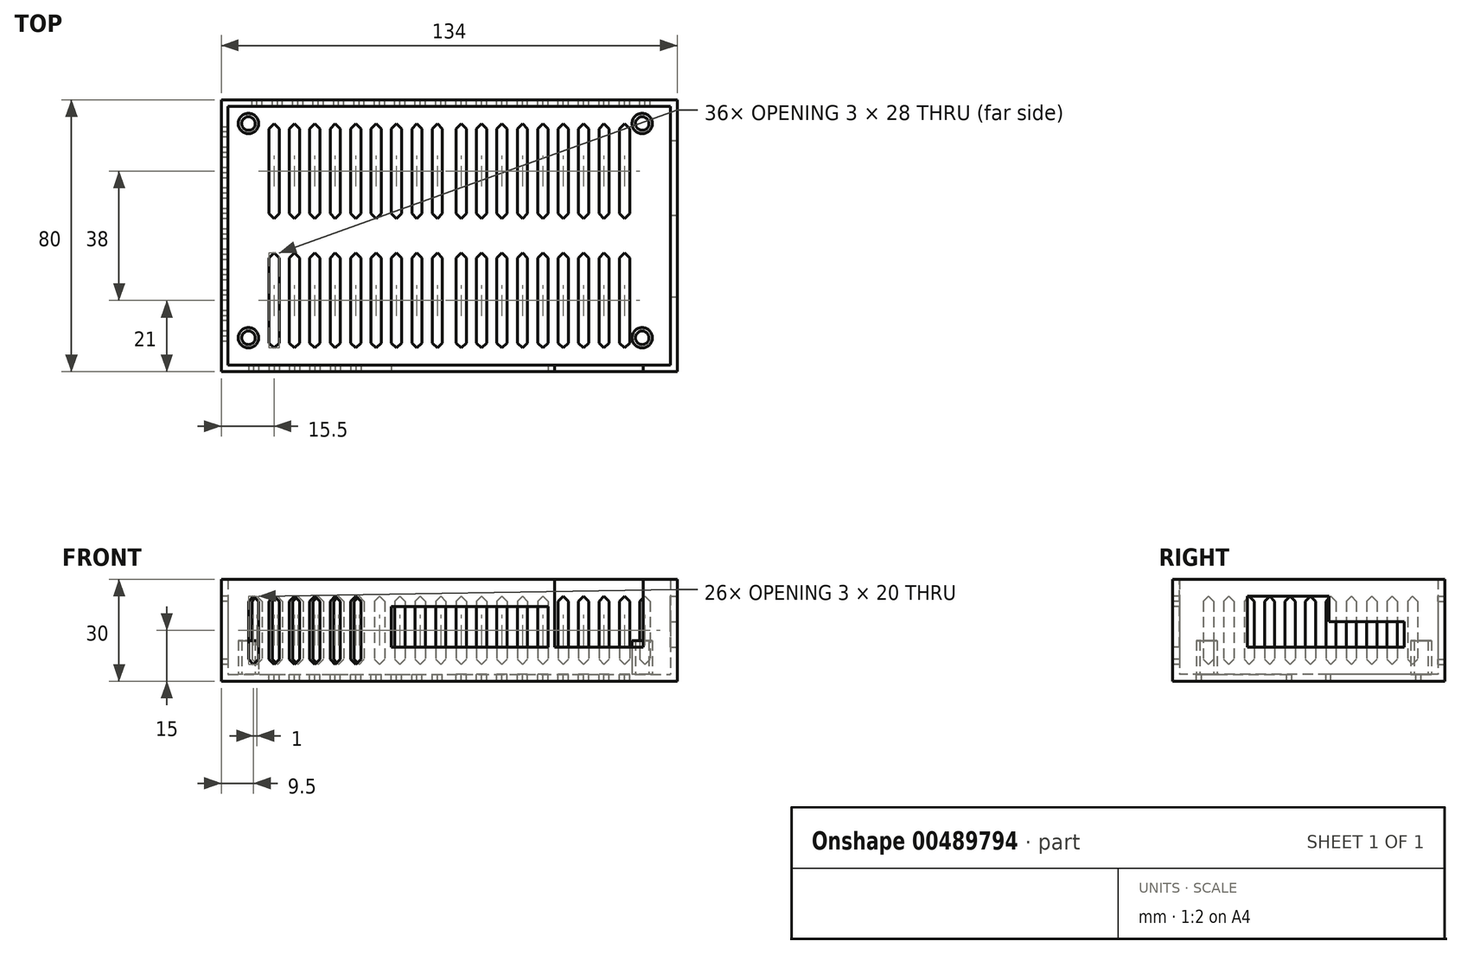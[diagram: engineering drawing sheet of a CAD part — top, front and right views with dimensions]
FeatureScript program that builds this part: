
annotation { "Feature Type Name" : "Feature", "Feature Type Description" : "" }
export const myFeature = defineFeature(function(context is Context, id is Id, definition is map)
    precondition{}
    {
        {
            var Q0;
            Q0=qCreatedBy(makeId("Top.planeOp"),FACE);
            var sketch = newSketch(context, id + "F0", { "sketchPlane" : qUnion([Q0])});
            skLineSegment(sketch, "E0.bottom", {"start": v(-65, 38) * mm, "end": v(65, 38) * mm});
            skLineSegment(sketch, "E0.top", {"start": v(-65, -38) * mm, "end": v(65, -38) * mm});
            skLineSegment(sketch, "E0.left", {"start": v(-65, 38) * mm, "end": v(-65, -38) * mm});
            skLineSegment(sketch, "E0.right", {"start": v(65, 38) * mm, "end": v(65, -38) * mm});
            skSolve(sketch);
        }
        {
            var Q0;
            Q0=makeQuery(id+"F0.imprint","IMPRINT",FACE,{"disambiguationData":[TD([[makeQuery(id+"F0.imprint","IMPRINT",EDGE,{"derivedFrom":sQuery(id+"F0.wireOp",EDGE,"E0.bottom")}),-1.0]])]});
            extrude(context, id + "F1", {"entities" : qUnion([Q0]), "depth" : 2 * mm});
        }
        {
            var Q0;
            Q0=qCreatedBy(makeId("Top.planeOp"),FACE);
            var sketch = newSketch(context, id + "F2", { "sketchPlane" : qUnion([Q0])});
            skLineSegment(sketch, "E1.bottom", {"start": v(-67, 40) * mm, "end": v(67, 40) * mm});
            skLineSegment(sketch, "E1.top", {"start": v(-67, -40) * mm, "end": v(67, -40) * mm});
            skLineSegment(sketch, "E1.left", {"start": v(-67, 40) * mm, "end": v(-67, -40) * mm});
            skLineSegment(sketch, "E1.right", {"start": v(67, 40) * mm, "end": v(67, -40) * mm});
            skLineSegment(sketch, "E2.bottom", {"start": v(-65, 38) * mm, "end": v(65, 38) * mm});
            skLineSegment(sketch, "E2.top", {"start": v(-65, -38) * mm, "end": v(65, -38) * mm});
            skLineSegment(sketch, "E2.left", {"start": v(-65, 38) * mm, "end": v(-65, -38) * mm});
            skLineSegment(sketch, "E2.right", {"start": v(65, 38) * mm, "end": v(65, -38) * mm});
            skSolve(sketch);
        }
        {
            var Q0;
            Q0=makeQuery(id+"F2.imprint","IMPRINT",FACE,{"disambiguationData":[TD([[makeQuery(id+"F2.imprint","IMPRINT",EDGE,{"derivedFrom":sQuery(id+"F2.wireOp",EDGE,"E1.bottom")}),-1.0]])]});
            extrude(context, id + "F3", {"entities" : qUnion([Q0]), "operationType" : NewBodyOperationType.ADD, "depth" : 30 * mm});
        }
        {
            var Q0;
            Q0=makeQuery(id+"F1.opExtrude","CAP_FACE",FACE,{"disambiguationData":[OSD([sQuery(id+"F0.wireOp",EDGE,"E0.bottom"),sQuery(id+"F0.wireOp",EDGE,"E0.top"),sQuery(id+"F0.wireOp",EDGE,"E0.left"),sQuery(id+"F0.wireOp",EDGE,"E0.right")])],"isStart":false});
            var sketch = newSketch(context, id + "F4", { "sketchPlane" : qUnion([Q0])});
            skCircle(sketch, "E3", {"center": v(-59, 33) * mm, "radius": 3 * mm});
            skCircle(sketch, "E4", {"center": v(56.7, 33) * mm, "radius": 3 * mm});
            skCircle(sketch, "E5", {"center": v(56.7, -30) * mm, "radius": 3 * mm});
            skCircle(sketch, "E6", {"center": v(-59, -30) * mm, "radius": 3 * mm});
            skCircle(sketch, "E7", {"center": v(-59, 33) * mm, "radius": 2 * mm});
            skCircle(sketch, "E8", {"center": v(-59, -30) * mm, "radius": 2 * mm});
            skCircle(sketch, "E9", {"center": v(56.7, -30) * mm, "radius": 2 * mm});
            skCircle(sketch, "E10", {"center": v(56.7, 33) * mm, "radius": 2 * mm});
            skSolve(sketch);
        }
        {
            var Q0;
            Q0=makeQuery(id+"F4.imprint","IMPRINT",FACE,{"disambiguationData":[TD([[makeQuery(id+"F4.imprint","IMPRINT",EDGE,{"derivedFrom":sQuery(id+"F4.wireOp",EDGE,"E4")}),1.0]])]});
            var Q1;
            Q1=makeQuery(id+"F4.imprint","IMPRINT",FACE,{"disambiguationData":[TD([[makeQuery(id+"F4.imprint","IMPRINT",EDGE,{"derivedFrom":sQuery(id+"F4.wireOp",EDGE,"E5")}),1.0]])]});
            var Q2;
            Q2=makeQuery(id+"F4.imprint","IMPRINT",FACE,{"disambiguationData":[TD([[makeQuery(id+"F4.imprint","IMPRINT",EDGE,{"derivedFrom":sQuery(id+"F4.wireOp",EDGE,"E6")}),1.0]])]});
            var Q3;
            Q3=makeQuery(id+"F4.imprint","IMPRINT",FACE,{"disambiguationData":[TD([[makeQuery(id+"F4.imprint","IMPRINT",EDGE,{"derivedFrom":sQuery(id+"F4.wireOp",EDGE,"E3")}),1.0]])]});
            extrude(context, id + "F5", {"entities" : qUnion([Q0, Q1, Q2, Q3]), "operationType" : NewBodyOperationType.ADD, "depth" : 10 * mm});
        }
        {
            var Q0;
            Q0=makeQuery(id+"F3.opExtrude","SWEPT_FACE",FACE,{"disambiguationData":[OSD([sQuery(id+"F2.wireOp",EDGE,"E1.top")])]});
            var sketch = newSketch(context, id + "F6", { "sketchPlane" : qUnion([Q0])});
            skLineSegment(sketch, "E11.bottom", {"start": v(31, 10) * mm, "end": v(57, 10) * mm});
            skLineSegment(sketch, "E11.top", {"start": v(31, 30) * mm, "end": v(57, 30) * mm});
            skLineSegment(sketch, "E11.left", {"start": v(31, 10) * mm, "end": v(31, 30) * mm});
            skLineSegment(sketch, "E11.right", {"start": v(57, 10) * mm, "end": v(57, 30) * mm});
            skLineSegment(sketch, "E12.bottom", {"start": v(-17, 10) * mm, "end": v(29, 10) * mm});
            skLineSegment(sketch, "E12.top", {"start": v(-17, 22) * mm, "end": v(29, 22) * mm});
            skLineSegment(sketch, "E12.left", {"start": v(-17, 10) * mm, "end": v(-17, 22) * mm});
            skLineSegment(sketch, "E12.right", {"start": v(29, 10) * mm, "end": v(29, 22) * mm});
            skSolve(sketch);
        }
        {
            var Q0;
            Q0=makeQuery(id+"F3.opExtrude","SWEPT_FACE",FACE,{"disambiguationData":[OSD([sQuery(id+"F2.wireOp",EDGE,"E1.right")])]});
            var sketch = newSketch(context, id + "F7", { "sketchPlane" : qUnion([Q0])});
            skLineSegment(sketch, "E13.bottom", {"start": v(-18, 10) * mm, "end": v(6, 10) * mm});
            skLineSegment(sketch, "E13.top", {"start": v(-18, 25) * mm, "end": v(6, 25) * mm});
            skLineSegment(sketch, "E13.left", {"start": v(-18, 10) * mm, "end": v(-18, 25) * mm});
            skLineSegment(sketch, "E13.right", {"start": v(6, 10) * mm, "end": v(6, 25) * mm});
            skLineSegment(sketch, "E14.bottom", {"start": v(6, 17.5) * mm, "end": v(28, 17.5) * mm});
            skLineSegment(sketch, "E14.top", {"start": v(6, 10) * mm, "end": v(28, 10) * mm});
            skLineSegment(sketch, "E14.left", {"start": v(6, 17.5) * mm, "end": v(6, 10) * mm});
            skLineSegment(sketch, "E14.right", {"start": v(28, 17.5) * mm, "end": v(28, 10) * mm});
            skSolve(sketch);
        }
        {
            var Q0;
            Q0=makeQuery(id+"F6.imprint","IMPRINT",FACE,{"disambiguationData":[TD([[makeQuery(id+"F6.imprint","IMPRINT",EDGE,{"derivedFrom":sQuery(id+"F6.wireOp",EDGE,"E11.bottom")}),1.0]])]});
            var Q1;
            Q1=makeQuery(id+"F6.imprint","IMPRINT",FACE,{"disambiguationData":[TD([[makeQuery(id+"F6.imprint","IMPRINT",EDGE,{"derivedFrom":sQuery(id+"F6.wireOp",EDGE,"E12.bottom")}),1.0]])]});
            extrude(context, id + "F8", {"entities" : qUnion([Q0, Q1]), "operationType" : NewBodyOperationType.REMOVE, "oppositeDirection" : true, "depth" : 2 * mm});
        }
        {
            var Q0;
            Q0=makeQuery(id+"F7.imprint","IMPRINT",FACE,{"disambiguationData":[TD([[makeQuery(id+"F7.imprint","IMPRINT",EDGE,{"derivedFrom":sQuery(id+"F7.wireOp",EDGE,"E13.bottom")}),1.0]])]});
            var Q1;
            Q1=makeQuery(id+"F7.imprint","IMPRINT",FACE,{"disambiguationData":[TD([[makeQuery(id+"F7.imprint","IMPRINT",EDGE,{"derivedFrom":sQuery(id+"F7.wireOp",EDGE,"E14.bottom")}),-1.0]])]});
            extrude(context, id + "F9", {"entities" : qUnion([Q0, Q1]), "operationType" : NewBodyOperationType.REMOVE, "oppositeDirection" : true, "depth" : 25 * mm});
        }
        {
            var Q0;
            Q0=makeQuery(id+"F3.opExtrude","SWEPT_FACE",FACE,{"disambiguationData":[OSD([sQuery(id+"F2.wireOp",EDGE,"E1.bottom")])]});
            var sketch = newSketch(context, id + "F10", { "sketchPlane" : qUnion([Q0])});
            skLineSegment(sketch, "E15.bottom", {"start": v(-59, 23.5) * mm, "end": v(-56, 23.5) * mm});
            skLineSegment(sketch, "E15.top", {"start": v(-59, 6.5) * mm, "end": v(-56, 6.5) * mm});
            skLineSegment(sketch, "E15.left", {"start": v(-59, 23.5) * mm, "end": v(-59, 6.5) * mm});
            skLineSegment(sketch, "E15.right", {"start": v(-56, 23.5) * mm, "end": v(-56, 6.5) * mm});
            skLineSegment(sketch, "E16", {"start": v(-59, 23.5) * mm, "end": v(-57.5, 25) * mm});
            skLineSegment(sketch, "E17", {"start": v(-57.5, 25) * mm, "end": v(-56, 23.5) * mm});
            skLineSegment(sketch, "E18", {"start": v(-56, 6.5) * mm, "end": v(-57.5, 5) * mm});
            skLineSegment(sketch, "E19", {"start": v(-57.5, 5) * mm, "end": v(-59, 6.5) * mm});
            skLineSegment(sketch, "E20.1.0.0", {"start": v(-53, 6.5) * mm, "end": v(-50, 6.5) * mm});
            skLineSegment(sketch, "E20.1.0.1", {"start": v(-50, 23.5) * mm, "end": v(-50, 6.5) * mm});
            skLineSegment(sketch, "E20.1.0.2", {"start": v(-53, 23.5) * mm, "end": v(-50, 23.5) * mm});
            skLineSegment(sketch, "E20.1.0.3", {"start": v(-53, 23.5) * mm, "end": v(-53, 6.5) * mm});
            skLineSegment(sketch, "E20.1.0.4", {"start": v(-51.5, 5) * mm, "end": v(-53, 6.5) * mm});
            skLineSegment(sketch, "E20.1.0.5", {"start": v(-53, 23.5) * mm, "end": v(-51.5, 25) * mm});
            skLineSegment(sketch, "E20.1.0.6", {"start": v(-51.5, 25) * mm, "end": v(-50, 23.5) * mm});
            skLineSegment(sketch, "E20.1.0.7", {"start": v(-50, 6.5) * mm, "end": v(-51.5, 5) * mm});
            skLineSegment(sketch, "E20.2.0.0", {"start": v(-47, 6.5) * mm, "end": v(-44, 6.5) * mm});
            skLineSegment(sketch, "E20.2.0.1", {"start": v(-44, 23.5) * mm, "end": v(-44, 6.5) * mm});
            skLineSegment(sketch, "E20.2.0.2", {"start": v(-47, 23.5) * mm, "end": v(-44, 23.5) * mm});
            skLineSegment(sketch, "E20.2.0.3", {"start": v(-47, 23.5) * mm, "end": v(-47, 6.5) * mm});
            skLineSegment(sketch, "E20.2.0.4", {"start": v(-45.5, 5) * mm, "end": v(-47, 6.5) * mm});
            skLineSegment(sketch, "E20.2.0.5", {"start": v(-47, 23.5) * mm, "end": v(-45.5, 25) * mm});
            skLineSegment(sketch, "E20.2.0.6", {"start": v(-45.5, 25) * mm, "end": v(-44, 23.5) * mm});
            skLineSegment(sketch, "E20.2.0.7", {"start": v(-44, 6.5) * mm, "end": v(-45.5, 5) * mm});
            skLineSegment(sketch, "E20.3.0.0", {"start": v(-41, 6.5) * mm, "end": v(-38, 6.5) * mm});
            skLineSegment(sketch, "E20.3.0.1", {"start": v(-38, 23.5) * mm, "end": v(-38, 6.5) * mm});
            skLineSegment(sketch, "E20.3.0.2", {"start": v(-41, 23.5) * mm, "end": v(-38, 23.5) * mm});
            skLineSegment(sketch, "E20.3.0.3", {"start": v(-41, 23.5) * mm, "end": v(-41, 6.5) * mm});
            skLineSegment(sketch, "E20.3.0.4", {"start": v(-39.5, 5) * mm, "end": v(-41, 6.5) * mm});
            skLineSegment(sketch, "E20.3.0.5", {"start": v(-41, 23.5) * mm, "end": v(-39.5, 25) * mm});
            skLineSegment(sketch, "E20.3.0.6", {"start": v(-39.5, 25) * mm, "end": v(-38, 23.5) * mm});
            skLineSegment(sketch, "E20.3.0.7", {"start": v(-38, 6.5) * mm, "end": v(-39.5, 5) * mm});
            skLineSegment(sketch, "E20.4.0.0", {"start": v(-35, 6.5) * mm, "end": v(-32, 6.5) * mm});
            skLineSegment(sketch, "E20.4.0.1", {"start": v(-32, 23.5) * mm, "end": v(-32, 6.5) * mm});
            skLineSegment(sketch, "E20.4.0.2", {"start": v(-35, 23.5) * mm, "end": v(-32, 23.5) * mm});
            skLineSegment(sketch, "E20.4.0.3", {"start": v(-35, 23.5) * mm, "end": v(-35, 6.5) * mm});
            skLineSegment(sketch, "E20.4.0.4", {"start": v(-33.5, 5) * mm, "end": v(-35, 6.5) * mm});
            skLineSegment(sketch, "E20.4.0.5", {"start": v(-35, 23.5) * mm, "end": v(-33.5, 25) * mm});
            skLineSegment(sketch, "E20.4.0.6", {"start": v(-33.5, 25) * mm, "end": v(-32, 23.5) * mm});
            skLineSegment(sketch, "E20.4.0.7", {"start": v(-32, 6.5) * mm, "end": v(-33.5, 5) * mm});
            skLineSegment(sketch, "E20.5.0.0", {"start": v(-29, 6.5) * mm, "end": v(-26, 6.5) * mm});
            skLineSegment(sketch, "E20.5.0.1", {"start": v(-26, 23.5) * mm, "end": v(-26, 6.5) * mm});
            skLineSegment(sketch, "E20.5.0.2", {"start": v(-29, 23.5) * mm, "end": v(-26, 23.5) * mm});
            skLineSegment(sketch, "E20.5.0.3", {"start": v(-29, 23.5) * mm, "end": v(-29, 6.5) * mm});
            skLineSegment(sketch, "E20.5.0.4", {"start": v(-27.5, 5) * mm, "end": v(-29, 6.5) * mm});
            skLineSegment(sketch, "E20.5.0.5", {"start": v(-29, 23.5) * mm, "end": v(-27.5, 25) * mm});
            skLineSegment(sketch, "E20.5.0.6", {"start": v(-27.5, 25) * mm, "end": v(-26, 23.5) * mm});
            skLineSegment(sketch, "E20.5.0.7", {"start": v(-26, 6.5) * mm, "end": v(-27.5, 5) * mm});
            skLineSegment(sketch, "E20.6.0.0", {"start": v(-23, 6.5) * mm, "end": v(-20, 6.5) * mm});
            skLineSegment(sketch, "E20.6.0.1", {"start": v(-20, 23.5) * mm, "end": v(-20, 6.5) * mm});
            skLineSegment(sketch, "E20.6.0.2", {"start": v(-23, 23.5) * mm, "end": v(-20, 23.5) * mm});
            skLineSegment(sketch, "E20.6.0.3", {"start": v(-23, 23.5) * mm, "end": v(-23, 6.5) * mm});
            skLineSegment(sketch, "E20.6.0.4", {"start": v(-21.5, 5) * mm, "end": v(-23, 6.5) * mm});
            skLineSegment(sketch, "E20.6.0.5", {"start": v(-23, 23.5) * mm, "end": v(-21.5, 25) * mm});
            skLineSegment(sketch, "E20.6.0.6", {"start": v(-21.5, 25) * mm, "end": v(-20, 23.5) * mm});
            skLineSegment(sketch, "E20.6.0.7", {"start": v(-20, 6.5) * mm, "end": v(-21.5, 5) * mm});
            skLineSegment(sketch, "E20.7.0.0", {"start": v(-17, 6.5) * mm, "end": v(-14, 6.5) * mm});
            skLineSegment(sketch, "E20.7.0.1", {"start": v(-14, 23.5) * mm, "end": v(-14, 6.5) * mm});
            skLineSegment(sketch, "E20.7.0.2", {"start": v(-17, 23.5) * mm, "end": v(-14, 23.5) * mm});
            skLineSegment(sketch, "E20.7.0.3", {"start": v(-17, 23.5) * mm, "end": v(-17, 6.5) * mm});
            skLineSegment(sketch, "E20.7.0.4", {"start": v(-15.5, 5) * mm, "end": v(-17, 6.5) * mm});
            skLineSegment(sketch, "E20.7.0.5", {"start": v(-17, 23.5) * mm, "end": v(-15.5, 25) * mm});
            skLineSegment(sketch, "E20.7.0.6", {"start": v(-15.5, 25) * mm, "end": v(-14, 23.5) * mm});
            skLineSegment(sketch, "E20.7.0.7", {"start": v(-14, 6.5) * mm, "end": v(-15.5, 5) * mm});
            skLineSegment(sketch, "E20.8.0.0", {"start": v(-11, 6.5) * mm, "end": v(-8, 6.5) * mm});
            skLineSegment(sketch, "E20.8.0.1", {"start": v(-8, 23.5) * mm, "end": v(-8, 6.5) * mm});
            skLineSegment(sketch, "E20.8.0.2", {"start": v(-11, 23.5) * mm, "end": v(-8, 23.5) * mm});
            skLineSegment(sketch, "E20.8.0.3", {"start": v(-11, 23.5) * mm, "end": v(-11, 6.5) * mm});
            skLineSegment(sketch, "E20.8.0.4", {"start": v(-9.5, 5) * mm, "end": v(-11, 6.5) * mm});
            skLineSegment(sketch, "E20.8.0.5", {"start": v(-11, 23.5) * mm, "end": v(-9.5, 25) * mm});
            skLineSegment(sketch, "E20.8.0.6", {"start": v(-9.5, 25) * mm, "end": v(-8, 23.5) * mm});
            skLineSegment(sketch, "E20.8.0.7", {"start": v(-8, 6.5) * mm, "end": v(-9.5, 5) * mm});
            skLineSegment(sketch, "E20.9.0.0", {"start": v(-5, 6.5) * mm, "end": v(-2, 6.5) * mm});
            skLineSegment(sketch, "E20.9.0.1", {"start": v(-2, 23.5) * mm, "end": v(-2, 6.5) * mm});
            skLineSegment(sketch, "E20.9.0.2", {"start": v(-5, 23.5) * mm, "end": v(-2, 23.5) * mm});
            skLineSegment(sketch, "E20.9.0.3", {"start": v(-5, 23.5) * mm, "end": v(-5, 6.5) * mm});
            skLineSegment(sketch, "E20.9.0.4", {"start": v(-3.5, 5) * mm, "end": v(-5, 6.5) * mm});
            skLineSegment(sketch, "E20.9.0.5", {"start": v(-5, 23.5) * mm, "end": v(-3.5, 25) * mm});
            skLineSegment(sketch, "E20.9.0.6", {"start": v(-3.5, 25) * mm, "end": v(-2, 23.5) * mm});
            skLineSegment(sketch, "E20.9.0.7", {"start": v(-2, 6.5) * mm, "end": v(-3.5, 5) * mm});
            skLineSegment(sketch, "E20.10.0.0", {"start": v(1, 6.5) * mm, "end": v(4, 6.5) * mm});
            skLineSegment(sketch, "E20.10.0.1", {"start": v(4, 23.5) * mm, "end": v(4, 6.5) * mm});
            skLineSegment(sketch, "E20.10.0.2", {"start": v(1, 23.5) * mm, "end": v(4, 23.5) * mm});
            skLineSegment(sketch, "E20.10.0.3", {"start": v(1, 23.5) * mm, "end": v(1, 6.5) * mm});
            skLineSegment(sketch, "E20.10.0.4", {"start": v(2.5, 5) * mm, "end": v(1, 6.5) * mm});
            skLineSegment(sketch, "E20.10.0.5", {"start": v(1, 23.5) * mm, "end": v(2.5, 25) * mm});
            skLineSegment(sketch, "E20.10.0.6", {"start": v(2.5, 25) * mm, "end": v(4, 23.5) * mm});
            skLineSegment(sketch, "E20.10.0.7", {"start": v(4, 6.5) * mm, "end": v(2.5, 5) * mm});
            skLineSegment(sketch, "E20.11.0.0", {"start": v(7, 6.5) * mm, "end": v(10, 6.5) * mm});
            skLineSegment(sketch, "E20.11.0.1", {"start": v(10, 23.5) * mm, "end": v(10, 6.5) * mm});
            skLineSegment(sketch, "E20.11.0.2", {"start": v(7, 23.5) * mm, "end": v(10, 23.5) * mm});
            skLineSegment(sketch, "E20.11.0.3", {"start": v(7, 23.5) * mm, "end": v(7, 6.5) * mm});
            skLineSegment(sketch, "E20.11.0.4", {"start": v(8.5, 5) * mm, "end": v(7, 6.5) * mm});
            skLineSegment(sketch, "E20.11.0.5", {"start": v(7, 23.5) * mm, "end": v(8.5, 25) * mm});
            skLineSegment(sketch, "E20.11.0.6", {"start": v(8.5, 25) * mm, "end": v(10, 23.5) * mm});
            skLineSegment(sketch, "E20.11.0.7", {"start": v(10, 6.5) * mm, "end": v(8.5, 5) * mm});
            skLineSegment(sketch, "E20.12.0.0", {"start": v(13, 6.5) * mm, "end": v(16, 6.5) * mm});
            skLineSegment(sketch, "E20.12.0.1", {"start": v(16, 23.5) * mm, "end": v(16, 6.5) * mm});
            skLineSegment(sketch, "E20.12.0.2", {"start": v(13, 23.5) * mm, "end": v(16, 23.5) * mm});
            skLineSegment(sketch, "E20.12.0.3", {"start": v(13, 23.5) * mm, "end": v(13, 6.5) * mm});
            skLineSegment(sketch, "E20.12.0.4", {"start": v(14.5, 5) * mm, "end": v(13, 6.5) * mm});
            skLineSegment(sketch, "E20.12.0.5", {"start": v(13, 23.5) * mm, "end": v(14.5, 25) * mm});
            skLineSegment(sketch, "E20.12.0.6", {"start": v(14.5, 25) * mm, "end": v(16, 23.5) * mm});
            skLineSegment(sketch, "E20.12.0.7", {"start": v(16, 6.5) * mm, "end": v(14.5, 5) * mm});
            skLineSegment(sketch, "E20.13.0.0", {"start": v(19, 6.5) * mm, "end": v(22, 6.5) * mm});
            skLineSegment(sketch, "E20.13.0.1", {"start": v(22, 23.5) * mm, "end": v(22, 6.5) * mm});
            skLineSegment(sketch, "E20.13.0.2", {"start": v(19, 23.5) * mm, "end": v(22, 23.5) * mm});
            skLineSegment(sketch, "E20.13.0.3", {"start": v(19, 23.5) * mm, "end": v(19, 6.5) * mm});
            skLineSegment(sketch, "E20.13.0.4", {"start": v(20.5, 5) * mm, "end": v(19, 6.5) * mm});
            skLineSegment(sketch, "E20.13.0.5", {"start": v(19, 23.5) * mm, "end": v(20.5, 25) * mm});
            skLineSegment(sketch, "E20.13.0.6", {"start": v(20.5, 25) * mm, "end": v(22, 23.5) * mm});
            skLineSegment(sketch, "E20.13.0.7", {"start": v(22, 6.5) * mm, "end": v(20.5, 5) * mm});
            skLineSegment(sketch, "E20.14.0.0", {"start": v(25, 6.5) * mm, "end": v(28, 6.5) * mm});
            skLineSegment(sketch, "E20.14.0.1", {"start": v(28, 23.5) * mm, "end": v(28, 6.5) * mm});
            skLineSegment(sketch, "E20.14.0.2", {"start": v(25, 23.5) * mm, "end": v(28, 23.5) * mm});
            skLineSegment(sketch, "E20.14.0.3", {"start": v(25, 23.5) * mm, "end": v(25, 6.5) * mm});
            skLineSegment(sketch, "E20.14.0.4", {"start": v(26.5, 5) * mm, "end": v(25, 6.5) * mm});
            skLineSegment(sketch, "E20.14.0.5", {"start": v(25, 23.5) * mm, "end": v(26.5, 25) * mm});
            skLineSegment(sketch, "E20.14.0.6", {"start": v(26.5, 25) * mm, "end": v(28, 23.5) * mm});
            skLineSegment(sketch, "E20.14.0.7", {"start": v(28, 6.5) * mm, "end": v(26.5, 5) * mm});
            skLineSegment(sketch, "E20.15.0.0", {"start": v(31, 6.5) * mm, "end": v(34, 6.5) * mm});
            skLineSegment(sketch, "E20.15.0.1", {"start": v(34, 23.5) * mm, "end": v(34, 6.5) * mm});
            skLineSegment(sketch, "E20.15.0.2", {"start": v(31, 23.5) * mm, "end": v(34, 23.5) * mm});
            skLineSegment(sketch, "E20.15.0.3", {"start": v(31, 23.5) * mm, "end": v(31, 6.5) * mm});
            skLineSegment(sketch, "E20.15.0.4", {"start": v(32.5, 5) * mm, "end": v(31, 6.5) * mm});
            skLineSegment(sketch, "E20.15.0.5", {"start": v(31, 23.5) * mm, "end": v(32.5, 25) * mm});
            skLineSegment(sketch, "E20.15.0.6", {"start": v(32.5, 25) * mm, "end": v(34, 23.5) * mm});
            skLineSegment(sketch, "E20.15.0.7", {"start": v(34, 6.5) * mm, "end": v(32.5, 5) * mm});
            skLineSegment(sketch, "E20.16.0.0", {"start": v(37, 6.5) * mm, "end": v(40, 6.5) * mm});
            skLineSegment(sketch, "E20.16.0.1", {"start": v(40, 23.5) * mm, "end": v(40, 6.5) * mm});
            skLineSegment(sketch, "E20.16.0.2", {"start": v(37, 23.5) * mm, "end": v(40, 23.5) * mm});
            skLineSegment(sketch, "E20.16.0.3", {"start": v(37, 23.5) * mm, "end": v(37, 6.5) * mm});
            skLineSegment(sketch, "E20.16.0.4", {"start": v(38.5, 5) * mm, "end": v(37, 6.5) * mm});
            skLineSegment(sketch, "E20.16.0.5", {"start": v(37, 23.5) * mm, "end": v(38.5, 25) * mm});
            skLineSegment(sketch, "E20.16.0.6", {"start": v(38.5, 25) * mm, "end": v(40, 23.5) * mm});
            skLineSegment(sketch, "E20.16.0.7", {"start": v(40, 6.5) * mm, "end": v(38.5, 5) * mm});
            skLineSegment(sketch, "E20.17.0.0", {"start": v(43, 6.5) * mm, "end": v(46, 6.5) * mm});
            skLineSegment(sketch, "E20.17.0.1", {"start": v(46, 23.5) * mm, "end": v(46, 6.5) * mm});
            skLineSegment(sketch, "E20.17.0.2", {"start": v(43, 23.5) * mm, "end": v(46, 23.5) * mm});
            skLineSegment(sketch, "E20.17.0.3", {"start": v(43, 23.5) * mm, "end": v(43, 6.5) * mm});
            skLineSegment(sketch, "E20.17.0.4", {"start": v(44.5, 5) * mm, "end": v(43, 6.5) * mm});
            skLineSegment(sketch, "E20.17.0.5", {"start": v(43, 23.5) * mm, "end": v(44.5, 25) * mm});
            skLineSegment(sketch, "E20.17.0.6", {"start": v(44.5, 25) * mm, "end": v(46, 23.5) * mm});
            skLineSegment(sketch, "E20.17.0.7", {"start": v(46, 6.5) * mm, "end": v(44.5, 5) * mm});
            skLineSegment(sketch, "E20.18.0.0", {"start": v(49, 6.5) * mm, "end": v(52, 6.5) * mm});
            skLineSegment(sketch, "E20.18.0.1", {"start": v(52, 23.5) * mm, "end": v(52, 6.5) * mm});
            skLineSegment(sketch, "E20.18.0.2", {"start": v(49, 23.5) * mm, "end": v(52, 23.5) * mm});
            skLineSegment(sketch, "E20.18.0.3", {"start": v(49, 23.5) * mm, "end": v(49, 6.5) * mm});
            skLineSegment(sketch, "E20.18.0.4", {"start": v(50.5, 5) * mm, "end": v(49, 6.5) * mm});
            skLineSegment(sketch, "E20.18.0.5", {"start": v(49, 23.5) * mm, "end": v(50.5, 25) * mm});
            skLineSegment(sketch, "E20.18.0.6", {"start": v(50.5, 25) * mm, "end": v(52, 23.5) * mm});
            skLineSegment(sketch, "E20.18.0.7", {"start": v(52, 6.5) * mm, "end": v(50.5, 5) * mm});
            skLineSegment(sketch, "E20.19.0.0", {"start": v(55, 6.5) * mm, "end": v(58, 6.5) * mm});
            skLineSegment(sketch, "E20.19.0.1", {"start": v(58, 23.5) * mm, "end": v(58, 6.5) * mm});
            skLineSegment(sketch, "E20.19.0.2", {"start": v(55, 23.5) * mm, "end": v(58, 23.5) * mm});
            skLineSegment(sketch, "E20.19.0.3", {"start": v(55, 23.5) * mm, "end": v(55, 6.5) * mm});
            skLineSegment(sketch, "E20.19.0.4", {"start": v(56.5, 5) * mm, "end": v(55, 6.5) * mm});
            skLineSegment(sketch, "E20.19.0.5", {"start": v(55, 23.5) * mm, "end": v(56.5, 25) * mm});
            skLineSegment(sketch, "E20.19.0.6", {"start": v(56.5, 25) * mm, "end": v(58, 23.5) * mm});
            skLineSegment(sketch, "E20.19.0.7", {"start": v(58, 6.5) * mm, "end": v(56.5, 5) * mm});
            skLineSegment(sketch, "E20.direction1", {"start": v(-57.5, 5) * mm, "end": v(-51.5, 5) * mm, "construction": true});
            skSolve(sketch);
        }
        {
            var Q0;
            Q0=qSketchRegion(id+"F10",true);
            extrude(context, id + "F11", {"entities" : qUnion([Q0]), "operationType" : NewBodyOperationType.REMOVE, "oppositeDirection" : true, "depth" : 2 * mm});
        }
        {
            var Q0;
            Q0=makeQuery(id+"F3.opExtrude","SWEPT_FACE",FACE,{"disambiguationData":[OSD([sQuery(id+"F2.wireOp",EDGE,"E1.left")])]});
            var sketch = newSketch(context, id + "F12", { "sketchPlane" : qUnion([Q0])});
            skLineSegment(sketch, "E21.bottom", {"start": v(-32, 23.5) * mm, "end": v(-29, 23.5) * mm});
            skLineSegment(sketch, "E21.top", {"start": v(-32, 6.5) * mm, "end": v(-29, 6.5) * mm});
            skLineSegment(sketch, "E21.left", {"start": v(-32, 23.5) * mm, "end": v(-32, 6.5) * mm});
            skLineSegment(sketch, "E21.right", {"start": v(-29, 23.5) * mm, "end": v(-29, 6.5) * mm});
            skLineSegment(sketch, "E22", {"start": v(-32, 23.5) * mm, "end": v(-30.5, 25) * mm});
            skLineSegment(sketch, "E23", {"start": v(-30.5, 25) * mm, "end": v(-29, 23.5) * mm});
            skLineSegment(sketch, "E24", {"start": v(-32, 6.5) * mm, "end": v(-30.5, 5) * mm});
            skLineSegment(sketch, "E25", {"start": v(-30.5, 5) * mm, "end": v(-29, 6.5) * mm});
            skLineSegment(sketch, "E26.1.0.0", {"start": v(-26, 23.5) * mm, "end": v(-23, 23.5) * mm});
            skLineSegment(sketch, "E26.1.0.1", {"start": v(-26, 6.5) * mm, "end": v(-23, 6.5) * mm});
            skLineSegment(sketch, "E26.1.0.2", {"start": v(-26, 23.5) * mm, "end": v(-26, 6.5) * mm});
            skLineSegment(sketch, "E26.1.0.3", {"start": v(-23, 23.5) * mm, "end": v(-23, 6.5) * mm});
            skLineSegment(sketch, "E26.1.0.4", {"start": v(-24.5, 5) * mm, "end": v(-23, 6.5) * mm});
            skLineSegment(sketch, "E26.1.0.5", {"start": v(-26, 23.5) * mm, "end": v(-24.5, 25) * mm});
            skLineSegment(sketch, "E26.1.0.6", {"start": v(-26, 6.5) * mm, "end": v(-24.5, 5) * mm});
            skLineSegment(sketch, "E26.1.0.7", {"start": v(-24.5, 25) * mm, "end": v(-23, 23.5) * mm});
            skLineSegment(sketch, "E26.2.0.0", {"start": v(-20, 23.5) * mm, "end": v(-17, 23.5) * mm});
            skLineSegment(sketch, "E26.2.0.1", {"start": v(-20, 6.5) * mm, "end": v(-17, 6.5) * mm});
            skLineSegment(sketch, "E26.2.0.2", {"start": v(-20, 23.5) * mm, "end": v(-20, 6.5) * mm});
            skLineSegment(sketch, "E26.2.0.3", {"start": v(-17, 23.5) * mm, "end": v(-17, 6.5) * mm});
            skLineSegment(sketch, "E26.2.0.4", {"start": v(-18.5, 5) * mm, "end": v(-17, 6.5) * mm});
            skLineSegment(sketch, "E26.2.0.5", {"start": v(-20, 23.5) * mm, "end": v(-18.5, 25) * mm});
            skLineSegment(sketch, "E26.2.0.6", {"start": v(-20, 6.5) * mm, "end": v(-18.5, 5) * mm});
            skLineSegment(sketch, "E26.2.0.7", {"start": v(-18.5, 25) * mm, "end": v(-17, 23.5) * mm});
            skLineSegment(sketch, "E26.3.0.0", {"start": v(-14, 23.5) * mm, "end": v(-11, 23.5) * mm});
            skLineSegment(sketch, "E26.3.0.1", {"start": v(-14, 6.5) * mm, "end": v(-11, 6.5) * mm});
            skLineSegment(sketch, "E26.3.0.2", {"start": v(-14, 23.5) * mm, "end": v(-14, 6.5) * mm});
            skLineSegment(sketch, "E26.3.0.3", {"start": v(-11, 23.5) * mm, "end": v(-11, 6.5) * mm});
            skLineSegment(sketch, "E26.3.0.4", {"start": v(-12.5, 5) * mm, "end": v(-11, 6.5) * mm});
            skLineSegment(sketch, "E26.3.0.5", {"start": v(-14, 23.5) * mm, "end": v(-12.5, 25) * mm});
            skLineSegment(sketch, "E26.3.0.6", {"start": v(-14, 6.5) * mm, "end": v(-12.5, 5) * mm});
            skLineSegment(sketch, "E26.3.0.7", {"start": v(-12.5, 25) * mm, "end": v(-11, 23.5) * mm});
            skLineSegment(sketch, "E26.4.0.0", {"start": v(-8, 23.5) * mm, "end": v(-5, 23.5) * mm});
            skLineSegment(sketch, "E26.4.0.1", {"start": v(-8, 6.5) * mm, "end": v(-5, 6.5) * mm});
            skLineSegment(sketch, "E26.4.0.2", {"start": v(-8, 23.5) * mm, "end": v(-8, 6.5) * mm});
            skLineSegment(sketch, "E26.4.0.3", {"start": v(-5, 23.5) * mm, "end": v(-5, 6.5) * mm});
            skLineSegment(sketch, "E26.4.0.4", {"start": v(-6.5, 5) * mm, "end": v(-5, 6.5) * mm});
            skLineSegment(sketch, "E26.4.0.5", {"start": v(-8, 23.5) * mm, "end": v(-6.5, 25) * mm});
            skLineSegment(sketch, "E26.4.0.6", {"start": v(-8, 6.5) * mm, "end": v(-6.5, 5) * mm});
            skLineSegment(sketch, "E26.4.0.7", {"start": v(-6.5, 25) * mm, "end": v(-5, 23.5) * mm});
            skLineSegment(sketch, "E26.5.0.0", {"start": v(-2, 23.5) * mm, "end": v(1, 23.5) * mm});
            skLineSegment(sketch, "E26.5.0.1", {"start": v(-2, 6.5) * mm, "end": v(1, 6.5) * mm});
            skLineSegment(sketch, "E26.5.0.2", {"start": v(-2, 23.5) * mm, "end": v(-2, 6.5) * mm});
            skLineSegment(sketch, "E26.5.0.3", {"start": v(1, 23.5) * mm, "end": v(1, 6.5) * mm});
            skLineSegment(sketch, "E26.5.0.4", {"start": v(-0.5, 5) * mm, "end": v(1, 6.5) * mm});
            skLineSegment(sketch, "E26.5.0.5", {"start": v(-2, 23.5) * mm, "end": v(-0.5, 25) * mm});
            skLineSegment(sketch, "E26.5.0.6", {"start": v(-2, 6.5) * mm, "end": v(-0.5, 5) * mm});
            skLineSegment(sketch, "E26.5.0.7", {"start": v(-0.5, 25) * mm, "end": v(1, 23.5) * mm});
            skLineSegment(sketch, "E26.6.0.0", {"start": v(4, 23.5) * mm, "end": v(7, 23.5) * mm});
            skLineSegment(sketch, "E26.6.0.1", {"start": v(4, 6.5) * mm, "end": v(7, 6.5) * mm});
            skLineSegment(sketch, "E26.6.0.2", {"start": v(4, 23.5) * mm, "end": v(4, 6.5) * mm});
            skLineSegment(sketch, "E26.6.0.3", {"start": v(7, 23.5) * mm, "end": v(7, 6.5) * mm});
            skLineSegment(sketch, "E26.6.0.4", {"start": v(5.5, 5) * mm, "end": v(7, 6.5) * mm});
            skLineSegment(sketch, "E26.6.0.5", {"start": v(4, 23.5) * mm, "end": v(5.5, 25) * mm});
            skLineSegment(sketch, "E26.6.0.6", {"start": v(4, 6.5) * mm, "end": v(5.5, 5) * mm});
            skLineSegment(sketch, "E26.6.0.7", {"start": v(5.5, 25) * mm, "end": v(7, 23.5) * mm});
            skLineSegment(sketch, "E26.7.0.0", {"start": v(10, 23.5) * mm, "end": v(13, 23.5) * mm});
            skLineSegment(sketch, "E26.7.0.1", {"start": v(10, 6.5) * mm, "end": v(13, 6.5) * mm});
            skLineSegment(sketch, "E26.7.0.2", {"start": v(10, 23.5) * mm, "end": v(10, 6.5) * mm});
            skLineSegment(sketch, "E26.7.0.3", {"start": v(13, 23.5) * mm, "end": v(13, 6.5) * mm});
            skLineSegment(sketch, "E26.7.0.4", {"start": v(11.5, 5) * mm, "end": v(13, 6.5) * mm});
            skLineSegment(sketch, "E26.7.0.5", {"start": v(10, 23.5) * mm, "end": v(11.5, 25) * mm});
            skLineSegment(sketch, "E26.7.0.6", {"start": v(10, 6.5) * mm, "end": v(11.5, 5) * mm});
            skLineSegment(sketch, "E26.7.0.7", {"start": v(11.5, 25) * mm, "end": v(13, 23.5) * mm});
            skLineSegment(sketch, "E26.8.0.0", {"start": v(16, 23.5) * mm, "end": v(19, 23.5) * mm});
            skLineSegment(sketch, "E26.8.0.1", {"start": v(16, 6.5) * mm, "end": v(19, 6.5) * mm});
            skLineSegment(sketch, "E26.8.0.2", {"start": v(16, 23.5) * mm, "end": v(16, 6.5) * mm});
            skLineSegment(sketch, "E26.8.0.3", {"start": v(19, 23.5) * mm, "end": v(19, 6.5) * mm});
            skLineSegment(sketch, "E26.8.0.4", {"start": v(17.5, 5) * mm, "end": v(19, 6.5) * mm});
            skLineSegment(sketch, "E26.8.0.5", {"start": v(16, 23.5) * mm, "end": v(17.5, 25) * mm});
            skLineSegment(sketch, "E26.8.0.6", {"start": v(16, 6.5) * mm, "end": v(17.5, 5) * mm});
            skLineSegment(sketch, "E26.8.0.7", {"start": v(17.5, 25) * mm, "end": v(19, 23.5) * mm});
            skLineSegment(sketch, "E26.9.0.0", {"start": v(22, 23.5) * mm, "end": v(25, 23.5) * mm});
            skLineSegment(sketch, "E26.9.0.1", {"start": v(22, 6.5) * mm, "end": v(25, 6.5) * mm});
            skLineSegment(sketch, "E26.9.0.2", {"start": v(22, 23.5) * mm, "end": v(22, 6.5) * mm});
            skLineSegment(sketch, "E26.9.0.3", {"start": v(25, 23.5) * mm, "end": v(25, 6.5) * mm});
            skLineSegment(sketch, "E26.9.0.4", {"start": v(23.5, 5) * mm, "end": v(25, 6.5) * mm});
            skLineSegment(sketch, "E26.9.0.5", {"start": v(22, 23.5) * mm, "end": v(23.5, 25) * mm});
            skLineSegment(sketch, "E26.9.0.6", {"start": v(22, 6.5) * mm, "end": v(23.5, 5) * mm});
            skLineSegment(sketch, "E26.9.0.7", {"start": v(23.5, 25) * mm, "end": v(25, 23.5) * mm});
            skLineSegment(sketch, "E26.10.0.0", {"start": v(28, 23.5) * mm, "end": v(31, 23.5) * mm});
            skLineSegment(sketch, "E26.10.0.1", {"start": v(28, 6.5) * mm, "end": v(31, 6.5) * mm});
            skLineSegment(sketch, "E26.10.0.2", {"start": v(28, 23.5) * mm, "end": v(28, 6.5) * mm});
            skLineSegment(sketch, "E26.10.0.3", {"start": v(31, 23.5) * mm, "end": v(31, 6.5) * mm});
            skLineSegment(sketch, "E26.10.0.4", {"start": v(29.5, 5) * mm, "end": v(31, 6.5) * mm});
            skLineSegment(sketch, "E26.10.0.5", {"start": v(28, 23.5) * mm, "end": v(29.5, 25) * mm});
            skLineSegment(sketch, "E26.10.0.6", {"start": v(28, 6.5) * mm, "end": v(29.5, 5) * mm});
            skLineSegment(sketch, "E26.10.0.7", {"start": v(29.5, 25) * mm, "end": v(31, 23.5) * mm});
            skLineSegment(sketch, "E26.direction1", {"start": v(-30.5, 5) * mm, "end": v(-24.5, 5) * mm, "construction": true});
            skSolve(sketch);
        }
        {
            var Q0;
            Q0=qSketchRegion(id+"F12",true);
            extrude(context, id + "F13", {"entities" : qUnion([Q0]), "operationType" : NewBodyOperationType.REMOVE, "oppositeDirection" : true, "depth" : 2 * mm});
        }
        {
            var Q0;
            Q0=makeQuery(id+"F3.opExtrude","SWEPT_FACE",FACE,{"disambiguationData":[OSD([sQuery(id+"F2.wireOp",EDGE,"E1.top")])]});
            var sketch = newSketch(context, id + "F14", { "sketchPlane" : qUnion([Q0])});
            skLineSegment(sketch, "E27.bottom", {"start": v(-59, 23.5) * mm, "end": v(-56, 23.5) * mm});
            skLineSegment(sketch, "E27.top", {"start": v(-59, 6.5) * mm, "end": v(-56, 6.5) * mm});
            skLineSegment(sketch, "E27.left", {"start": v(-59, 23.5) * mm, "end": v(-59, 6.5) * mm});
            skLineSegment(sketch, "E27.right", {"start": v(-56, 23.5) * mm, "end": v(-56, 6.5) * mm});
            skLineSegment(sketch, "E28", {"start": v(-59, 23.5) * mm, "end": v(-57.5, 25) * mm});
            skLineSegment(sketch, "E29", {"start": v(-57.5, 25) * mm, "end": v(-56, 23.5) * mm});
            skLineSegment(sketch, "E30", {"start": v(-59, 6.5) * mm, "end": v(-57.5, 5) * mm});
            skLineSegment(sketch, "E31", {"start": v(-57.5, 5) * mm, "end": v(-56, 6.5) * mm});
            skLineSegment(sketch, "E32.1.0.0", {"start": v(-53, 23.5) * mm, "end": v(-53, 6.5) * mm});
            skLineSegment(sketch, "E32.1.0.1", {"start": v(-50, 23.5) * mm, "end": v(-50, 6.5) * mm});
            skLineSegment(sketch, "E32.1.0.2", {"start": v(-53, 23.5) * mm, "end": v(-51.5, 25) * mm});
            skLineSegment(sketch, "E32.1.0.3", {"start": v(-53, 6.5) * mm, "end": v(-50, 6.5) * mm});
            skLineSegment(sketch, "E32.1.0.4", {"start": v(-53, 23.5) * mm, "end": v(-50, 23.5) * mm});
            skLineSegment(sketch, "E32.1.0.5", {"start": v(-51.5, 25) * mm, "end": v(-50, 23.5) * mm});
            skLineSegment(sketch, "E32.1.0.6", {"start": v(-53, 6.5) * mm, "end": v(-51.5, 5) * mm});
            skLineSegment(sketch, "E32.1.0.7", {"start": v(-51.5, 5) * mm, "end": v(-50, 6.5) * mm});
            skLineSegment(sketch, "E32.2.0.0", {"start": v(-47, 23.5) * mm, "end": v(-47, 6.5) * mm});
            skLineSegment(sketch, "E32.2.0.1", {"start": v(-44, 23.5) * mm, "end": v(-44, 6.5) * mm});
            skLineSegment(sketch, "E32.2.0.2", {"start": v(-47, 23.5) * mm, "end": v(-45.5, 25) * mm});
            skLineSegment(sketch, "E32.2.0.3", {"start": v(-47, 6.5) * mm, "end": v(-44, 6.5) * mm});
            skLineSegment(sketch, "E32.2.0.4", {"start": v(-47, 23.5) * mm, "end": v(-44, 23.5) * mm});
            skLineSegment(sketch, "E32.2.0.5", {"start": v(-45.5, 25) * mm, "end": v(-44, 23.5) * mm});
            skLineSegment(sketch, "E32.2.0.6", {"start": v(-47, 6.5) * mm, "end": v(-45.5, 5) * mm});
            skLineSegment(sketch, "E32.2.0.7", {"start": v(-45.5, 5) * mm, "end": v(-44, 6.5) * mm});
            skLineSegment(sketch, "E32.3.0.0", {"start": v(-41, 23.5) * mm, "end": v(-41, 6.5) * mm});
            skLineSegment(sketch, "E32.3.0.1", {"start": v(-38, 23.5) * mm, "end": v(-38, 6.5) * mm});
            skLineSegment(sketch, "E32.3.0.2", {"start": v(-41, 23.5) * mm, "end": v(-39.5, 25) * mm});
            skLineSegment(sketch, "E32.3.0.3", {"start": v(-41, 6.5) * mm, "end": v(-38, 6.5) * mm});
            skLineSegment(sketch, "E32.3.0.4", {"start": v(-41, 23.5) * mm, "end": v(-38, 23.5) * mm});
            skLineSegment(sketch, "E32.3.0.5", {"start": v(-39.5, 25) * mm, "end": v(-38, 23.5) * mm});
            skLineSegment(sketch, "E32.3.0.6", {"start": v(-41, 6.5) * mm, "end": v(-39.5, 5) * mm});
            skLineSegment(sketch, "E32.3.0.7", {"start": v(-39.5, 5) * mm, "end": v(-38, 6.5) * mm});
            skLineSegment(sketch, "E32.4.0.0", {"start": v(-35, 23.5) * mm, "end": v(-35, 6.5) * mm});
            skLineSegment(sketch, "E32.4.0.1", {"start": v(-32, 23.5) * mm, "end": v(-32, 6.5) * mm});
            skLineSegment(sketch, "E32.4.0.2", {"start": v(-35, 23.5) * mm, "end": v(-33.5, 25) * mm});
            skLineSegment(sketch, "E32.4.0.3", {"start": v(-35, 6.5) * mm, "end": v(-32, 6.5) * mm});
            skLineSegment(sketch, "E32.4.0.4", {"start": v(-35, 23.5) * mm, "end": v(-32, 23.5) * mm});
            skLineSegment(sketch, "E32.4.0.5", {"start": v(-33.5, 25) * mm, "end": v(-32, 23.5) * mm});
            skLineSegment(sketch, "E32.4.0.6", {"start": v(-35, 6.5) * mm, "end": v(-33.5, 5) * mm});
            skLineSegment(sketch, "E32.4.0.7", {"start": v(-33.5, 5) * mm, "end": v(-32, 6.5) * mm});
            skLineSegment(sketch, "E32.5.0.0", {"start": v(-29, 23.5) * mm, "end": v(-29, 6.5) * mm});
            skLineSegment(sketch, "E32.5.0.1", {"start": v(-26, 23.5) * mm, "end": v(-26, 6.5) * mm});
            skLineSegment(sketch, "E32.5.0.2", {"start": v(-29, 23.5) * mm, "end": v(-27.5, 25) * mm});
            skLineSegment(sketch, "E32.5.0.3", {"start": v(-29, 6.5) * mm, "end": v(-26, 6.5) * mm});
            skLineSegment(sketch, "E32.5.0.4", {"start": v(-29, 23.5) * mm, "end": v(-26, 23.5) * mm});
            skLineSegment(sketch, "E32.5.0.5", {"start": v(-27.5, 25) * mm, "end": v(-26, 23.5) * mm});
            skLineSegment(sketch, "E32.5.0.6", {"start": v(-29, 6.5) * mm, "end": v(-27.5, 5) * mm});
            skLineSegment(sketch, "E32.5.0.7", {"start": v(-27.5, 5) * mm, "end": v(-26, 6.5) * mm});
            skLineSegment(sketch, "E32.direction1", {"start": v(-57.5, 5) * mm, "end": v(-51.5, 5) * mm, "construction": true});
            skSolve(sketch);
        }
        {
            var Q0;
            Q0=qSketchRegion(id+"F14",true);
            extrude(context, id + "F15", {"entities" : qUnion([Q0]), "operationType" : NewBodyOperationType.REMOVE, "oppositeDirection" : true, "depth" : 2 * mm});
        }
        {
            var Q0;
            Q0=makeQuery(id+"F5.boolean.opBoolean","SPLIT",FACE,{"disambiguationData":[TD([makeQuery(id+"F3.opExtrude","SWEPT_FACE",FACE,{"disambiguationData":[OSD([sQuery(id+"F2.wireOp",EDGE,"E2.bottom")])]})])],"derivedFrom":makeQuery(id+"F1.opExtrude","CAP_FACE",FACE,{"disambiguationData":[OSD([sQuery(id+"F0.wireOp",EDGE,"E0.bottom"),sQuery(id+"F0.wireOp",EDGE,"E0.top"),sQuery(id+"F0.wireOp",EDGE,"E0.left"),sQuery(id+"F0.wireOp",EDGE,"E0.right")])],"isStart":false})});
            var sketch = newSketch(context, id + "F16", { "sketchPlane" : qUnion([Q0])});
            skLineSegment(sketch, "E33.bottom", {"start": v(-53, 31.5) * mm, "end": v(-50, 31.5) * mm});
            skLineSegment(sketch, "E33.top", {"start": v(-53, 6.5) * mm, "end": v(-50, 6.5) * mm});
            skLineSegment(sketch, "E33.left", {"start": v(-53, 31.5) * mm, "end": v(-53, 6.5) * mm});
            skLineSegment(sketch, "E33.right", {"start": v(-50, 31.5) * mm, "end": v(-50, 6.5) * mm});
            skLineSegment(sketch, "E34", {"start": v(-53, 6.5) * mm, "end": v(-51.5, 5) * mm});
            skLineSegment(sketch, "E35", {"start": v(-51.5, 5) * mm, "end": v(-50, 6.5) * mm});
            skLineSegment(sketch, "E36", {"start": v(-53, 31.5) * mm, "end": v(-51.5, 33) * mm});
            skLineSegment(sketch, "E37", {"start": v(-51.5, 33) * mm, "end": v(-50, 31.5) * mm});
            skLineSegment(sketch, "E38.1.0.0", {"start": v(-47, 31.5) * mm, "end": v(-47, 6.5) * mm});
            skLineSegment(sketch, "E38.1.0.1", {"start": v(-44, 31.5) * mm, "end": v(-44, 6.5) * mm});
            skLineSegment(sketch, "E38.1.0.2", {"start": v(-45.5, 33) * mm, "end": v(-44, 31.5) * mm});
            skLineSegment(sketch, "E38.1.0.3", {"start": v(-47, 31.5) * mm, "end": v(-44, 31.5) * mm});
            skLineSegment(sketch, "E38.1.0.4", {"start": v(-47, 6.5) * mm, "end": v(-44, 6.5) * mm});
            skLineSegment(sketch, "E38.1.0.5", {"start": v(-47, 6.5) * mm, "end": v(-45.5, 5) * mm});
            skLineSegment(sketch, "E38.1.0.6", {"start": v(-47, 31.5) * mm, "end": v(-45.5, 33) * mm});
            skLineSegment(sketch, "E38.1.0.7", {"start": v(-45.5, 5) * mm, "end": v(-44, 6.5) * mm});
            skLineSegment(sketch, "E38.2.0.0", {"start": v(-41, 31.5) * mm, "end": v(-41, 6.5) * mm});
            skLineSegment(sketch, "E38.2.0.1", {"start": v(-38, 31.5) * mm, "end": v(-38, 6.5) * mm});
            skLineSegment(sketch, "E38.2.0.2", {"start": v(-39.5, 33) * mm, "end": v(-38, 31.5) * mm});
            skLineSegment(sketch, "E38.2.0.3", {"start": v(-41, 31.5) * mm, "end": v(-38, 31.5) * mm});
            skLineSegment(sketch, "E38.2.0.4", {"start": v(-41, 6.5) * mm, "end": v(-38, 6.5) * mm});
            skLineSegment(sketch, "E38.2.0.5", {"start": v(-41, 6.5) * mm, "end": v(-39.5, 5) * mm});
            skLineSegment(sketch, "E38.2.0.6", {"start": v(-41, 31.5) * mm, "end": v(-39.5, 33) * mm});
            skLineSegment(sketch, "E38.2.0.7", {"start": v(-39.5, 5) * mm, "end": v(-38, 6.5) * mm});
            skLineSegment(sketch, "E38.3.0.0", {"start": v(-35, 31.5) * mm, "end": v(-35, 6.5) * mm});
            skLineSegment(sketch, "E38.3.0.1", {"start": v(-32, 31.5) * mm, "end": v(-32, 6.5) * mm});
            skLineSegment(sketch, "E38.3.0.2", {"start": v(-33.5, 33) * mm, "end": v(-32, 31.5) * mm});
            skLineSegment(sketch, "E38.3.0.3", {"start": v(-35, 31.5) * mm, "end": v(-32, 31.5) * mm});
            skLineSegment(sketch, "E38.3.0.4", {"start": v(-35, 6.5) * mm, "end": v(-32, 6.5) * mm});
            skLineSegment(sketch, "E38.3.0.5", {"start": v(-35, 6.5) * mm, "end": v(-33.5, 5) * mm});
            skLineSegment(sketch, "E38.3.0.6", {"start": v(-35, 31.5) * mm, "end": v(-33.5, 33) * mm});
            skLineSegment(sketch, "E38.3.0.7", {"start": v(-33.5, 5) * mm, "end": v(-32, 6.5) * mm});
            skLineSegment(sketch, "E38.4.0.0", {"start": v(-29, 31.5) * mm, "end": v(-29, 6.5) * mm});
            skLineSegment(sketch, "E38.4.0.1", {"start": v(-26, 31.5) * mm, "end": v(-26, 6.5) * mm});
            skLineSegment(sketch, "E38.4.0.2", {"start": v(-27.5, 33) * mm, "end": v(-26, 31.5) * mm});
            skLineSegment(sketch, "E38.4.0.3", {"start": v(-29, 31.5) * mm, "end": v(-26, 31.5) * mm});
            skLineSegment(sketch, "E38.4.0.4", {"start": v(-29, 6.5) * mm, "end": v(-26, 6.5) * mm});
            skLineSegment(sketch, "E38.4.0.5", {"start": v(-29, 6.5) * mm, "end": v(-27.5, 5) * mm});
            skLineSegment(sketch, "E38.4.0.6", {"start": v(-29, 31.5) * mm, "end": v(-27.5, 33) * mm});
            skLineSegment(sketch, "E38.4.0.7", {"start": v(-27.5, 5) * mm, "end": v(-26, 6.5) * mm});
            skLineSegment(sketch, "E38.5.0.0", {"start": v(-23, 31.5) * mm, "end": v(-23, 6.5) * mm});
            skLineSegment(sketch, "E38.5.0.1", {"start": v(-20, 31.5) * mm, "end": v(-20, 6.5) * mm});
            skLineSegment(sketch, "E38.5.0.2", {"start": v(-21.5, 33) * mm, "end": v(-20, 31.5) * mm});
            skLineSegment(sketch, "E38.5.0.3", {"start": v(-23, 31.5) * mm, "end": v(-20, 31.5) * mm});
            skLineSegment(sketch, "E38.5.0.4", {"start": v(-23, 6.5) * mm, "end": v(-20, 6.5) * mm});
            skLineSegment(sketch, "E38.5.0.5", {"start": v(-23, 6.5) * mm, "end": v(-21.5, 5) * mm});
            skLineSegment(sketch, "E38.5.0.6", {"start": v(-23, 31.5) * mm, "end": v(-21.5, 33) * mm});
            skLineSegment(sketch, "E38.5.0.7", {"start": v(-21.5, 5) * mm, "end": v(-20, 6.5) * mm});
            skLineSegment(sketch, "E38.6.0.0", {"start": v(-17, 31.5) * mm, "end": v(-17, 6.5) * mm});
            skLineSegment(sketch, "E38.6.0.1", {"start": v(-14, 31.5) * mm, "end": v(-14, 6.5) * mm});
            skLineSegment(sketch, "E38.6.0.2", {"start": v(-15.5, 33) * mm, "end": v(-14, 31.5) * mm});
            skLineSegment(sketch, "E38.6.0.3", {"start": v(-17, 31.5) * mm, "end": v(-14, 31.5) * mm});
            skLineSegment(sketch, "E38.6.0.4", {"start": v(-17, 6.5) * mm, "end": v(-14, 6.5) * mm});
            skLineSegment(sketch, "E38.6.0.5", {"start": v(-17, 6.5) * mm, "end": v(-15.5, 5) * mm});
            skLineSegment(sketch, "E38.6.0.6", {"start": v(-17, 31.5) * mm, "end": v(-15.5, 33) * mm});
            skLineSegment(sketch, "E38.6.0.7", {"start": v(-15.5, 5) * mm, "end": v(-14, 6.5) * mm});
            skLineSegment(sketch, "E38.7.0.0", {"start": v(-11, 31.5) * mm, "end": v(-11, 6.5) * mm});
            skLineSegment(sketch, "E38.7.0.1", {"start": v(-8, 31.5) * mm, "end": v(-8, 6.5) * mm});
            skLineSegment(sketch, "E38.7.0.2", {"start": v(-9.5, 33) * mm, "end": v(-8, 31.5) * mm});
            skLineSegment(sketch, "E38.7.0.3", {"start": v(-11, 31.5) * mm, "end": v(-8, 31.5) * mm});
            skLineSegment(sketch, "E38.7.0.4", {"start": v(-11, 6.5) * mm, "end": v(-8, 6.5) * mm});
            skLineSegment(sketch, "E38.7.0.5", {"start": v(-11, 6.5) * mm, "end": v(-9.5, 5) * mm});
            skLineSegment(sketch, "E38.7.0.6", {"start": v(-11, 31.5) * mm, "end": v(-9.5, 33) * mm});
            skLineSegment(sketch, "E38.7.0.7", {"start": v(-9.5, 5) * mm, "end": v(-8, 6.5) * mm});
            skLineSegment(sketch, "E38.8.0.0", {"start": v(-5, 31.5) * mm, "end": v(-5, 6.5) * mm});
            skLineSegment(sketch, "E38.8.0.1", {"start": v(-2, 31.5) * mm, "end": v(-2, 6.5) * mm});
            skLineSegment(sketch, "E38.8.0.2", {"start": v(-3.5, 33) * mm, "end": v(-2, 31.5) * mm});
            skLineSegment(sketch, "E38.8.0.3", {"start": v(-5, 31.5) * mm, "end": v(-2, 31.5) * mm});
            skLineSegment(sketch, "E38.8.0.4", {"start": v(-5, 6.5) * mm, "end": v(-2, 6.5) * mm});
            skLineSegment(sketch, "E38.8.0.5", {"start": v(-5, 6.5) * mm, "end": v(-3.5, 5) * mm});
            skLineSegment(sketch, "E38.8.0.6", {"start": v(-5, 31.5) * mm, "end": v(-3.5, 33) * mm});
            skLineSegment(sketch, "E38.8.0.7", {"start": v(-3.5, 5) * mm, "end": v(-2, 6.5) * mm});
            skLineSegment(sketch, "E38.direction1", {"start": v(-51.5, 5) * mm, "end": v(-45.5, 5) * mm, "construction": true});
            skLineSegment(sketch, "E39.MirrorCS", {"start": v(11, 6.5) * mm, "end": v(8, 6.5) * mm});
            skLineSegment(sketch, "E40.MirrorCS", {"start": v(53, 6.5) * mm, "end": v(51.5, 5) * mm});
            skLineSegment(sketch, "E41.MirrorCS", {"start": v(33.5, 33) * mm, "end": v(32, 31.5) * mm});
            skLineSegment(sketch, "E42.MirrorCS", {"start": v(51.5, 5) * mm, "end": v(50, 6.5) * mm});
            skLineSegment(sketch, "E43.MirrorCS", {"start": v(9.5, 33) * mm, "end": v(8, 31.5) * mm});
            skLineSegment(sketch, "E44.MirrorCS", {"start": v(27.5, 5) * mm, "end": v(26, 6.5) * mm});
            skLineSegment(sketch, "E45.MirrorCS", {"start": v(15.5, 5) * mm, "end": v(14, 6.5) * mm});
            skLineSegment(sketch, "E46.MirrorCS", {"start": v(53, 6.5) * mm, "end": v(50, 6.5) * mm});
            skLineSegment(sketch, "E47.MirrorCS", {"start": v(53, 31.5) * mm, "end": v(50, 31.5) * mm});
            skLineSegment(sketch, "E48.MirrorCS", {"start": v(35, 6.5) * mm, "end": v(32, 6.5) * mm});
            skLineSegment(sketch, "E49.MirrorCS", {"start": v(21.5, 33) * mm, "end": v(20, 31.5) * mm});
            skLineSegment(sketch, "E50.MirrorCS", {"start": v(53, 31.5) * mm, "end": v(51.5, 33) * mm});
            skLineSegment(sketch, "E51.MirrorCS", {"start": v(3.5, 5) * mm, "end": v(2, 6.5) * mm});
            skLineSegment(sketch, "E52.MirrorCS", {"start": v(41, 31.5) * mm, "end": v(38, 31.5) * mm});
            skLineSegment(sketch, "E53.MirrorCS", {"start": v(29, 31.5) * mm, "end": v(26, 31.5) * mm});
            skLineSegment(sketch, "E54.MirrorCS", {"start": v(39.5, 33) * mm, "end": v(38, 31.5) * mm});
            skLineSegment(sketch, "E55.MirrorCS", {"start": v(15.5, 33) * mm, "end": v(14, 31.5) * mm});
            skLineSegment(sketch, "E56.MirrorCS", {"start": v(45.5, 33) * mm, "end": v(44, 31.5) * mm});
            skLineSegment(sketch, "E57.MirrorCS", {"start": v(17, 6.5) * mm, "end": v(15.5, 5) * mm});
            skLineSegment(sketch, "E58.MirrorCS", {"start": v(47, 6.5) * mm, "end": v(45.5, 5) * mm});
            skLineSegment(sketch, "E59.MirrorCS", {"start": v(21.5, 5) * mm, "end": v(20, 6.5) * mm});
            skLineSegment(sketch, "E60.MirrorCS", {"start": v(23, 31.5) * mm, "end": v(20, 31.5) * mm});
            skLineSegment(sketch, "E61.MirrorCS", {"start": v(41, 6.5) * mm, "end": v(39.5, 5) * mm});
            skLineSegment(sketch, "E62.MirrorCS", {"start": v(5, 31.5) * mm, "end": v(2, 31.5) * mm});
            skLineSegment(sketch, "E63.MirrorCS", {"start": v(11, 6.5) * mm, "end": v(9.5, 5) * mm});
            skLineSegment(sketch, "E64.MirrorCS", {"start": v(5, 6.5) * mm, "end": v(2, 6.5) * mm});
            skLineSegment(sketch, "E65.MirrorCS", {"start": v(39.5, 5) * mm, "end": v(38, 6.5) * mm});
            skLineSegment(sketch, "E66.MirrorCS", {"start": v(47, 6.5) * mm, "end": v(44, 6.5) * mm});
            skLineSegment(sketch, "E67.MirrorCS", {"start": v(33.5, 5) * mm, "end": v(32, 6.5) * mm});
            skLineSegment(sketch, "E68.MirrorCS", {"start": v(41, 31.5) * mm, "end": v(39.5, 33) * mm});
            skLineSegment(sketch, "E69.MirrorCS", {"start": v(9.5, 5) * mm, "end": v(8, 6.5) * mm});
            skLineSegment(sketch, "E70.MirrorCS", {"start": v(5, 31.5) * mm, "end": v(3.5, 33) * mm});
            skLineSegment(sketch, "E71.MirrorCS", {"start": v(29, 6.5) * mm, "end": v(27.5, 5) * mm});
            skLineSegment(sketch, "E72.MirrorCS", {"start": v(47, 31.5) * mm, "end": v(44, 31.5) * mm});
            skLineSegment(sketch, "E73.MirrorCS", {"start": v(11, 31.5) * mm, "end": v(8, 31.5) * mm});
            skLineSegment(sketch, "E74.MirrorCS", {"start": v(35, 31.5) * mm, "end": v(32, 31.5) * mm});
            skLineSegment(sketch, "E75.MirrorCS", {"start": v(41, 6.5) * mm, "end": v(38, 6.5) * mm});
            skLineSegment(sketch, "E76.MirrorCS", {"start": v(17, 31.5) * mm, "end": v(14, 31.5) * mm});
            skLineSegment(sketch, "E77.MirrorCS", {"start": v(29, 6.5) * mm, "end": v(26, 6.5) * mm});
            skLineSegment(sketch, "E78.MirrorCS", {"start": v(29, 31.5) * mm, "end": v(27.5, 33) * mm});
            skLineSegment(sketch, "E79.MirrorCS", {"start": v(3.5, 33) * mm, "end": v(2, 31.5) * mm});
            skLineSegment(sketch, "E80.MirrorCS", {"start": v(5, 6.5) * mm, "end": v(3.5, 5) * mm});
            skLineSegment(sketch, "E81.MirrorCS", {"start": v(17, 31.5) * mm, "end": v(15.5, 33) * mm});
            skLineSegment(sketch, "E82.MirrorCS", {"start": v(17, 6.5) * mm, "end": v(14, 6.5) * mm});
            skLineSegment(sketch, "E83.MirrorCS", {"start": v(23, 6.5) * mm, "end": v(21.5, 5) * mm});
            skLineSegment(sketch, "E84.MirrorCS", {"start": v(23, 6.5) * mm, "end": v(20, 6.5) * mm});
            skLineSegment(sketch, "E85.MirrorCS", {"start": v(35, 6.5) * mm, "end": v(33.5, 5) * mm});
            skLineSegment(sketch, "E86.MirrorCS", {"start": v(11, 31.5) * mm, "end": v(9.5, 33) * mm});
            skLineSegment(sketch, "E87.MirrorCS", {"start": v(45.5, 5) * mm, "end": v(44, 6.5) * mm});
            skLineSegment(sketch, "E88.MirrorCS", {"start": v(51.5, 33) * mm, "end": v(50, 31.5) * mm});
            skLineSegment(sketch, "E89.MirrorCS", {"start": v(27.5, 33) * mm, "end": v(26, 31.5) * mm});
            skLineSegment(sketch, "E90.MirrorCS", {"start": v(47, 31.5) * mm, "end": v(45.5, 33) * mm});
            skLineSegment(sketch, "E91.MirrorCS", {"start": v(35, 31.5) * mm, "end": v(33.5, 33) * mm});
            skLineSegment(sketch, "E92.MirrorCS", {"start": v(23, 31.5) * mm, "end": v(21.5, 33) * mm});
            skLineSegment(sketch, "E93.MirrorCS", {"start": v(5, 31.5) * mm, "end": v(5, 6.5) * mm});
            skLineSegment(sketch, "E94.MirrorCS", {"start": v(50, 31.5) * mm, "end": v(50, 6.5) * mm});
            skLineSegment(sketch, "E95.MirrorCS", {"start": v(53, 31.5) * mm, "end": v(53, 6.5) * mm});
            skLineSegment(sketch, "E96.MirrorCS", {"start": v(29, 31.5) * mm, "end": v(29, 6.5) * mm});
            skLineSegment(sketch, "E97.MirrorCS", {"start": v(17, 31.5) * mm, "end": v(17, 6.5) * mm});
            skLineSegment(sketch, "E98.MirrorCS", {"start": v(14, 31.5) * mm, "end": v(14, 6.5) * mm});
            skLineSegment(sketch, "E99.MirrorCS", {"start": v(26, 31.5) * mm, "end": v(26, 6.5) * mm});
            skLineSegment(sketch, "E100.MirrorCS", {"start": v(38, 31.5) * mm, "end": v(38, 6.5) * mm});
            skLineSegment(sketch, "E101.MirrorCS", {"start": v(2, 31.5) * mm, "end": v(2, 6.5) * mm});
            skLineSegment(sketch, "E102.MirrorCS", {"start": v(8, 31.5) * mm, "end": v(8, 6.5) * mm});
            skLineSegment(sketch, "E103.MirrorCS", {"start": v(47, 31.5) * mm, "end": v(47, 6.5) * mm});
            skLineSegment(sketch, "E104.MirrorCS", {"start": v(44, 31.5) * mm, "end": v(44, 6.5) * mm});
            skLineSegment(sketch, "E105.MirrorCS", {"start": v(23, 31.5) * mm, "end": v(23, 6.5) * mm});
            skLineSegment(sketch, "E106.MirrorCS", {"start": v(11, 31.5) * mm, "end": v(11, 6.5) * mm});
            skLineSegment(sketch, "E107.MirrorCS", {"start": v(51.5, 5) * mm, "end": v(45.5, 5) * mm, "construction": true});
            skLineSegment(sketch, "E108.MirrorCS", {"start": v(35, 31.5) * mm, "end": v(35, 6.5) * mm});
            skLineSegment(sketch, "E109.MirrorCS", {"start": v(41, 31.5) * mm, "end": v(41, 6.5) * mm});
            skLineSegment(sketch, "E110.MirrorCS", {"start": v(20, 31.5) * mm, "end": v(20, 6.5) * mm});
            skLineSegment(sketch, "E111.MirrorCS", {"start": v(32, 31.5) * mm, "end": v(32, 6.5) * mm});
            skLineSegment(sketch, "E112.MirrorCS", {"start": v(-41, -6.5) * mm, "end": v(-39.5, -5) * mm});
            skLineSegment(sketch, "E113.MirrorCS", {"start": v(-45.5, -33) * mm, "end": v(-44, -31.5) * mm});
            skLineSegment(sketch, "E114.MirrorCS", {"start": v(-23, -6.5) * mm, "end": v(-21.5, -5) * mm});
            skLineSegment(sketch, "E115.MirrorCS", {"start": v(-5, -31.5) * mm, "end": v(-2, -31.5) * mm});
            skLineSegment(sketch, "E116.MirrorCS", {"start": v(21.5, -33) * mm, "end": v(20, -31.5) * mm});
            skLineSegment(sketch, "E117.MirrorCS", {"start": v(-11, -31.5) * mm, "end": v(-8, -31.5) * mm});
            skLineSegment(sketch, "E118.MirrorCS", {"start": v(-35, -6.5) * mm, "end": v(-33.5, -5) * mm});
            skLineSegment(sketch, "E119.MirrorCS", {"start": v(-47, -31.5) * mm, "end": v(-44, -31.5) * mm});
            skLineSegment(sketch, "E120.MirrorCS", {"start": v(-23, -31.5) * mm, "end": v(-20, -31.5) * mm});
            skLineSegment(sketch, "E121.MirrorCS", {"start": v(39.5, -5) * mm, "end": v(38, -6.5) * mm});
            skLineSegment(sketch, "E122.MirrorCS", {"start": v(17, -31.5) * mm, "end": v(15.5, -33) * mm});
            skLineSegment(sketch, "E123.MirrorCS", {"start": v(29, -31.5) * mm, "end": v(26, -31.5) * mm});
            skLineSegment(sketch, "E124.MirrorCS", {"start": v(-41, -31.5) * mm, "end": v(-38, -31.5) * mm});
            skLineSegment(sketch, "E125.MirrorCS", {"start": v(-29, -31.5) * mm, "end": v(-26, -31.5) * mm});
            skLineSegment(sketch, "E126.MirrorCS", {"start": v(-9.5, -5) * mm, "end": v(-8, -6.5) * mm});
            skLineSegment(sketch, "E127.MirrorCS", {"start": v(9.5, -33) * mm, "end": v(8, -31.5) * mm});
            skLineSegment(sketch, "E128.MirrorCS", {"start": v(35, -6.5) * mm, "end": v(33.5, -5) * mm});
            skLineSegment(sketch, "E129.MirrorCS", {"start": v(-17, -31.5) * mm, "end": v(-14, -31.5) * mm});
            skLineSegment(sketch, "E130.MirrorCS", {"start": v(-17, -6.5) * mm, "end": v(-14, -6.5) * mm});
            skLineSegment(sketch, "E131.MirrorCS", {"start": v(-29, -6.5) * mm, "end": v(-26, -6.5) * mm});
            skLineSegment(sketch, "E132.MirrorCS", {"start": v(-41, -6.5) * mm, "end": v(-38, -6.5) * mm});
            skLineSegment(sketch, "E133.MirrorCS", {"start": v(27.5, -33) * mm, "end": v(26, -31.5) * mm});
            skLineSegment(sketch, "E134.MirrorCS", {"start": v(9.5, -5) * mm, "end": v(8, -6.5) * mm});
            skLineSegment(sketch, "E135.MirrorCS", {"start": v(15.5, -5) * mm, "end": v(14, -6.5) * mm});
            skLineSegment(sketch, "E136.MirrorCS", {"start": v(41, -6.5) * mm, "end": v(39.5, -5) * mm});
            skLineSegment(sketch, "E137.MirrorCS", {"start": v(29, -6.5) * mm, "end": v(26, -6.5) * mm});
            skLineSegment(sketch, "E138.MirrorCS", {"start": v(-39.5, -5) * mm, "end": v(-38, -6.5) * mm});
            skLineSegment(sketch, "E139.MirrorCS", {"start": v(-33.5, -5) * mm, "end": v(-32, -6.5) * mm});
            skLineSegment(sketch, "E140.MirrorCS", {"start": v(-21.5, -5) * mm, "end": v(-20, -6.5) * mm});
            skLineSegment(sketch, "E141.MirrorCS", {"start": v(35, -31.5) * mm, "end": v(32, -31.5) * mm});
            skLineSegment(sketch, "E142.MirrorCS", {"start": v(47, -31.5) * mm, "end": v(45.5, -33) * mm});
            skLineSegment(sketch, "E143.MirrorCS", {"start": v(-23, -6.5) * mm, "end": v(-20, -6.5) * mm});
            skLineSegment(sketch, "E144.MirrorCS", {"start": v(39.5, -33) * mm, "end": v(38, -31.5) * mm});
            skLineSegment(sketch, "E145.MirrorCS", {"start": v(-11, -6.5) * mm, "end": v(-8, -6.5) * mm});
            skLineSegment(sketch, "E146.MirrorCS", {"start": v(51.5, -5) * mm, "end": v(50, -6.5) * mm});
            skLineSegment(sketch, "E147.MirrorCS", {"start": v(47, -6.5) * mm, "end": v(45.5, -5) * mm});
            skLineSegment(sketch, "E148.MirrorCS", {"start": v(-51.5, -5) * mm, "end": v(-45.5, -5) * mm, "construction": true});
            skLineSegment(sketch, "E149.MirrorCS", {"start": v(47, -31.5) * mm, "end": v(44, -31.5) * mm});
            skLineSegment(sketch, "E150.MirrorCS", {"start": v(11, -31.5) * mm, "end": v(8, -31.5) * mm});
            skLineSegment(sketch, "E151.MirrorCS", {"start": v(17, -6.5) * mm, "end": v(14, -6.5) * mm});
            skLineSegment(sketch, "E152.MirrorCS", {"start": v(-53, -31.5) * mm, "end": v(-51.5, -33) * mm});
            skLineSegment(sketch, "E153.MirrorCS", {"start": v(-35, -6.5) * mm, "end": v(-32, -6.5) * mm});
            skLineSegment(sketch, "E154.MirrorCS", {"start": v(47, -6.5) * mm, "end": v(44, -6.5) * mm});
            skLineSegment(sketch, "E155.MirrorCS", {"start": v(-3.5, -33) * mm, "end": v(-2, -31.5) * mm});
            skLineSegment(sketch, "E156.MirrorCS", {"start": v(35, -6.5) * mm, "end": v(32, -6.5) * mm});
            skLineSegment(sketch, "E157.MirrorCS", {"start": v(5, -6.5) * mm, "end": v(2, -6.5) * mm});
            skLineSegment(sketch, "E158.MirrorCS", {"start": v(5, -6.5) * mm, "end": v(3.5, -5) * mm});
            skLineSegment(sketch, "E159.MirrorCS", {"start": v(53, -31.5) * mm, "end": v(51.5, -33) * mm});
            skLineSegment(sketch, "E160.MirrorCS", {"start": v(-5, -6.5) * mm, "end": v(-2, -6.5) * mm});
            skLineSegment(sketch, "E161.MirrorCS", {"start": v(-39.5, -33) * mm, "end": v(-38, -31.5) * mm});
            skLineSegment(sketch, "E162.MirrorCS", {"start": v(-27.5, -33) * mm, "end": v(-26, -31.5) * mm});
            skLineSegment(sketch, "E163.MirrorCS", {"start": v(-21.5, -33) * mm, "end": v(-20, -31.5) * mm});
            skLineSegment(sketch, "E164.MirrorCS", {"start": v(-15.5, -33) * mm, "end": v(-14, -31.5) * mm});
            skLineSegment(sketch, "E165.MirrorCS", {"start": v(-9.5, -33) * mm, "end": v(-8, -31.5) * mm});
            skLineSegment(sketch, "E166.MirrorCS", {"start": v(21.5, -5) * mm, "end": v(20, -6.5) * mm});
            skLineSegment(sketch, "E167.MirrorCS", {"start": v(33.5, -33) * mm, "end": v(32, -31.5) * mm});
            skLineSegment(sketch, "E168.MirrorCS", {"start": v(45.5, -5) * mm, "end": v(44, -6.5) * mm});
            skLineSegment(sketch, "E169.MirrorCS", {"start": v(-3.5, -5) * mm, "end": v(-2, -6.5) * mm});
            skLineSegment(sketch, "E170.MirrorCS", {"start": v(-5, -31.5) * mm, "end": v(-3.5, -33) * mm});
            skLineSegment(sketch, "E171.MirrorCS", {"start": v(15.5, -33) * mm, "end": v(14, -31.5) * mm});
            skLineSegment(sketch, "E172.MirrorCS", {"start": v(-15.5, -5) * mm, "end": v(-14, -6.5) * mm});
            skLineSegment(sketch, "E173.MirrorCS", {"start": v(41, -31.5) * mm, "end": v(39.5, -33) * mm});
            skLineSegment(sketch, "E174.MirrorCS", {"start": v(23, -6.5) * mm, "end": v(20, -6.5) * mm});
            skLineSegment(sketch, "E175.MirrorCS", {"start": v(-53, -31.5) * mm, "end": v(-50, -31.5) * mm});
            skLineSegment(sketch, "E176.MirrorCS", {"start": v(-45.5, -5) * mm, "end": v(-44, -6.5) * mm});
            skLineSegment(sketch, "E177.MirrorCS", {"start": v(-27.5, -5) * mm, "end": v(-26, -6.5) * mm});
            skLineSegment(sketch, "E178.MirrorCS", {"start": v(17, -6.5) * mm, "end": v(15.5, -5) * mm});
            skLineSegment(sketch, "E179.MirrorCS", {"start": v(-41, -31.5) * mm, "end": v(-39.5, -33) * mm});
            skLineSegment(sketch, "E180.MirrorCS", {"start": v(-53, -6.5) * mm, "end": v(-50, -6.5) * mm});
            skLineSegment(sketch, "E181.MirrorCS", {"start": v(-47, -6.5) * mm, "end": v(-44, -6.5) * mm});
            skLineSegment(sketch, "E182.MirrorCS", {"start": v(3.5, -33) * mm, "end": v(2, -31.5) * mm});
            skLineSegment(sketch, "E183.MirrorCS", {"start": v(-35, -31.5) * mm, "end": v(-32, -31.5) * mm});
            skLineSegment(sketch, "E184.MirrorCS", {"start": v(23, -31.5) * mm, "end": v(21.5, -33) * mm});
            skLineSegment(sketch, "E185.MirrorCS", {"start": v(-17, -31.5) * mm, "end": v(-15.5, -33) * mm});
            skLineSegment(sketch, "E186.MirrorCS", {"start": v(11, -6.5) * mm, "end": v(9.5, -5) * mm});
            skLineSegment(sketch, "E187.MirrorCS", {"start": v(53, -31.5) * mm, "end": v(50, -31.5) * mm});
            skLineSegment(sketch, "E188.MirrorCS", {"start": v(23, -31.5) * mm, "end": v(20, -31.5) * mm});
            skLineSegment(sketch, "E189.MirrorCS", {"start": v(-33.5, -33) * mm, "end": v(-32, -31.5) * mm});
            skLineSegment(sketch, "E190.MirrorCS", {"start": v(17, -31.5) * mm, "end": v(14, -31.5) * mm});
            skLineSegment(sketch, "E191.MirrorCS", {"start": v(-11, -6.5) * mm, "end": v(-9.5, -5) * mm});
            skLineSegment(sketch, "E192.MirrorCS", {"start": v(41, -31.5) * mm, "end": v(38, -31.5) * mm});
            skLineSegment(sketch, "E193.MirrorCS", {"start": v(11, -6.5) * mm, "end": v(8, -6.5) * mm});
            skLineSegment(sketch, "E194.MirrorCS", {"start": v(51.5, -5) * mm, "end": v(45.5, -5) * mm, "construction": true});
            skLineSegment(sketch, "E195.MirrorCS", {"start": v(-53, -6.5) * mm, "end": v(-51.5, -5) * mm});
            skLineSegment(sketch, "E196.MirrorCS", {"start": v(-35, -31.5) * mm, "end": v(-33.5, -33) * mm});
            skLineSegment(sketch, "E197.MirrorCS", {"start": v(-5, -6.5) * mm, "end": v(-3.5, -5) * mm});
            skLineSegment(sketch, "E198.MirrorCS", {"start": v(3.5, -5) * mm, "end": v(2, -6.5) * mm});
            skLineSegment(sketch, "E199.MirrorCS", {"start": v(35, -31.5) * mm, "end": v(33.5, -33) * mm});
            skLineSegment(sketch, "E200.MirrorCS", {"start": v(-47, -6.5) * mm, "end": v(-45.5, -5) * mm});
            skLineSegment(sketch, "E201.MirrorCS", {"start": v(45.5, -33) * mm, "end": v(44, -31.5) * mm});
            skLineSegment(sketch, "E202.MirrorCS", {"start": v(-29, -31.5) * mm, "end": v(-27.5, -33) * mm});
            skLineSegment(sketch, "E203.MirrorCS", {"start": v(27.5, -5) * mm, "end": v(26, -6.5) * mm});
            skLineSegment(sketch, "E204.MirrorCS", {"start": v(33.5, -5) * mm, "end": v(32, -6.5) * mm});
            skLineSegment(sketch, "E205.MirrorCS", {"start": v(23, -6.5) * mm, "end": v(21.5, -5) * mm});
            skLineSegment(sketch, "E206.MirrorCS", {"start": v(-29, -6.5) * mm, "end": v(-27.5, -5) * mm});
            skLineSegment(sketch, "E207.MirrorCS", {"start": v(-17, -6.5) * mm, "end": v(-15.5, -5) * mm});
            skLineSegment(sketch, "E208.MirrorCS", {"start": v(29, -6.5) * mm, "end": v(27.5, -5) * mm});
            skLineSegment(sketch, "E209.MirrorCS", {"start": v(-23, -31.5) * mm, "end": v(-21.5, -33) * mm});
            skLineSegment(sketch, "E210.MirrorCS", {"start": v(-51.5, -5) * mm, "end": v(-50, -6.5) * mm});
            skLineSegment(sketch, "E211.MirrorCS", {"start": v(29, -31.5) * mm, "end": v(27.5, -33) * mm});
            skLineSegment(sketch, "E212.MirrorCS", {"start": v(53, -6.5) * mm, "end": v(50, -6.5) * mm});
            skLineSegment(sketch, "E213.MirrorCS", {"start": v(5, -31.5) * mm, "end": v(2, -31.5) * mm});
            skLineSegment(sketch, "E214.MirrorCS", {"start": v(5, -31.5) * mm, "end": v(3.5, -33) * mm});
            skLineSegment(sketch, "E215.MirrorCS", {"start": v(41, -6.5) * mm, "end": v(38, -6.5) * mm});
            skLineSegment(sketch, "E216.MirrorCS", {"start": v(-47, -31.5) * mm, "end": v(-45.5, -33) * mm});
            skLineSegment(sketch, "E217.MirrorCS", {"start": v(53, -6.5) * mm, "end": v(51.5, -5) * mm});
            skLineSegment(sketch, "E218.MirrorCS", {"start": v(11, -31.5) * mm, "end": v(9.5, -33) * mm});
            skLineSegment(sketch, "E219.MirrorCS", {"start": v(-51.5, -33) * mm, "end": v(-50, -31.5) * mm});
            skLineSegment(sketch, "E220.MirrorCS", {"start": v(51.5, -33) * mm, "end": v(50, -31.5) * mm});
            skLineSegment(sketch, "E221.MirrorCS", {"start": v(-11, -31.5) * mm, "end": v(-9.5, -33) * mm});
            skLineSegment(sketch, "E222.MirrorCS", {"start": v(-44, -31.5) * mm, "end": v(-44, -6.5) * mm});
            skLineSegment(sketch, "E223.MirrorCS", {"start": v(8, -31.5) * mm, "end": v(8, -6.5) * mm});
            skLineSegment(sketch, "E224.MirrorCS", {"start": v(17, -31.5) * mm, "end": v(17, -6.5) * mm});
            skLineSegment(sketch, "E225.MirrorCS", {"start": v(-20, -31.5) * mm, "end": v(-20, -6.5) * mm});
            skLineSegment(sketch, "E226.MirrorCS", {"start": v(23, -31.5) * mm, "end": v(23, -6.5) * mm});
            skLineSegment(sketch, "E227.MirrorCS", {"start": v(5, -31.5) * mm, "end": v(5, -6.5) * mm});
            skLineSegment(sketch, "E228.MirrorCS", {"start": v(41, -31.5) * mm, "end": v(41, -6.5) * mm});
            skLineSegment(sketch, "E229.MirrorCS", {"start": v(2, -31.5) * mm, "end": v(2, -6.5) * mm});
            skLineSegment(sketch, "E230.MirrorCS", {"start": v(-47, -31.5) * mm, "end": v(-47, -6.5) * mm});
            skLineSegment(sketch, "E231.MirrorCS", {"start": v(11, -31.5) * mm, "end": v(11, -6.5) * mm});
            skLineSegment(sketch, "E232.MirrorCS", {"start": v(29, -31.5) * mm, "end": v(29, -6.5) * mm});
            skLineSegment(sketch, "E233.MirrorCS", {"start": v(-35, -31.5) * mm, "end": v(-35, -6.5) * mm});
            skLineSegment(sketch, "E234.MirrorCS", {"start": v(-8, -31.5) * mm, "end": v(-8, -6.5) * mm});
            skLineSegment(sketch, "E235.MirrorCS", {"start": v(-23, -31.5) * mm, "end": v(-23, -6.5) * mm});
            skLineSegment(sketch, "E236.MirrorCS", {"start": v(44, -31.5) * mm, "end": v(44, -6.5) * mm});
            skLineSegment(sketch, "E237.MirrorCS", {"start": v(14, -31.5) * mm, "end": v(14, -6.5) * mm});
            skLineSegment(sketch, "E238.MirrorCS", {"start": v(35, -31.5) * mm, "end": v(35, -6.5) * mm});
            skLineSegment(sketch, "E239.MirrorCS", {"start": v(38, -31.5) * mm, "end": v(38, -6.5) * mm});
            skLineSegment(sketch, "E240.MirrorCS", {"start": v(-41, -31.5) * mm, "end": v(-41, -6.5) * mm});
            skLineSegment(sketch, "E241.MirrorCS", {"start": v(-14, -31.5) * mm, "end": v(-14, -6.5) * mm});
            skLineSegment(sketch, "E242.MirrorCS", {"start": v(-26, -31.5) * mm, "end": v(-26, -6.5) * mm});
            skLineSegment(sketch, "E243.MirrorCS", {"start": v(-29, -31.5) * mm, "end": v(-29, -6.5) * mm});
            skLineSegment(sketch, "E244.MirrorCS", {"start": v(-17, -31.5) * mm, "end": v(-17, -6.5) * mm});
            skLineSegment(sketch, "E245.MirrorCS", {"start": v(-38, -31.5) * mm, "end": v(-38, -6.5) * mm});
            skLineSegment(sketch, "E246.MirrorCS", {"start": v(-50, -31.5) * mm, "end": v(-50, -6.5) * mm});
            skLineSegment(sketch, "E247.MirrorCS", {"start": v(-2, -31.5) * mm, "end": v(-2, -6.5) * mm});
            skLineSegment(sketch, "E248.MirrorCS", {"start": v(32, -31.5) * mm, "end": v(32, -6.5) * mm});
            skLineSegment(sketch, "E249.MirrorCS", {"start": v(-53, -31.5) * mm, "end": v(-53, -6.5) * mm});
            skLineSegment(sketch, "E250.MirrorCS", {"start": v(53, -31.5) * mm, "end": v(53, -6.5) * mm});
            skLineSegment(sketch, "E251.MirrorCS", {"start": v(26, -31.5) * mm, "end": v(26, -6.5) * mm});
            skLineSegment(sketch, "E252.MirrorCS", {"start": v(-32, -31.5) * mm, "end": v(-32, -6.5) * mm});
            skLineSegment(sketch, "E253.MirrorCS", {"start": v(-11, -31.5) * mm, "end": v(-11, -6.5) * mm});
            skLineSegment(sketch, "E254.MirrorCS", {"start": v(50, -31.5) * mm, "end": v(50, -6.5) * mm});
            skLineSegment(sketch, "E255.MirrorCS", {"start": v(47, -31.5) * mm, "end": v(47, -6.5) * mm});
            skLineSegment(sketch, "E256.MirrorCS", {"start": v(-5, -31.5) * mm, "end": v(-5, -6.5) * mm});
            skLineSegment(sketch, "E257.MirrorCS", {"start": v(20, -31.5) * mm, "end": v(20, -6.5) * mm});
            skSolve(sketch);
        }
        {
            var Q0;
            Q0=qSketchRegion(id+"F16",true);
            extrude(context, id + "F17", {"entities" : qUnion([Q0]), "operationType" : NewBodyOperationType.REMOVE, "oppositeDirection" : true, "depth" : 2 * mm});
        }
    });
